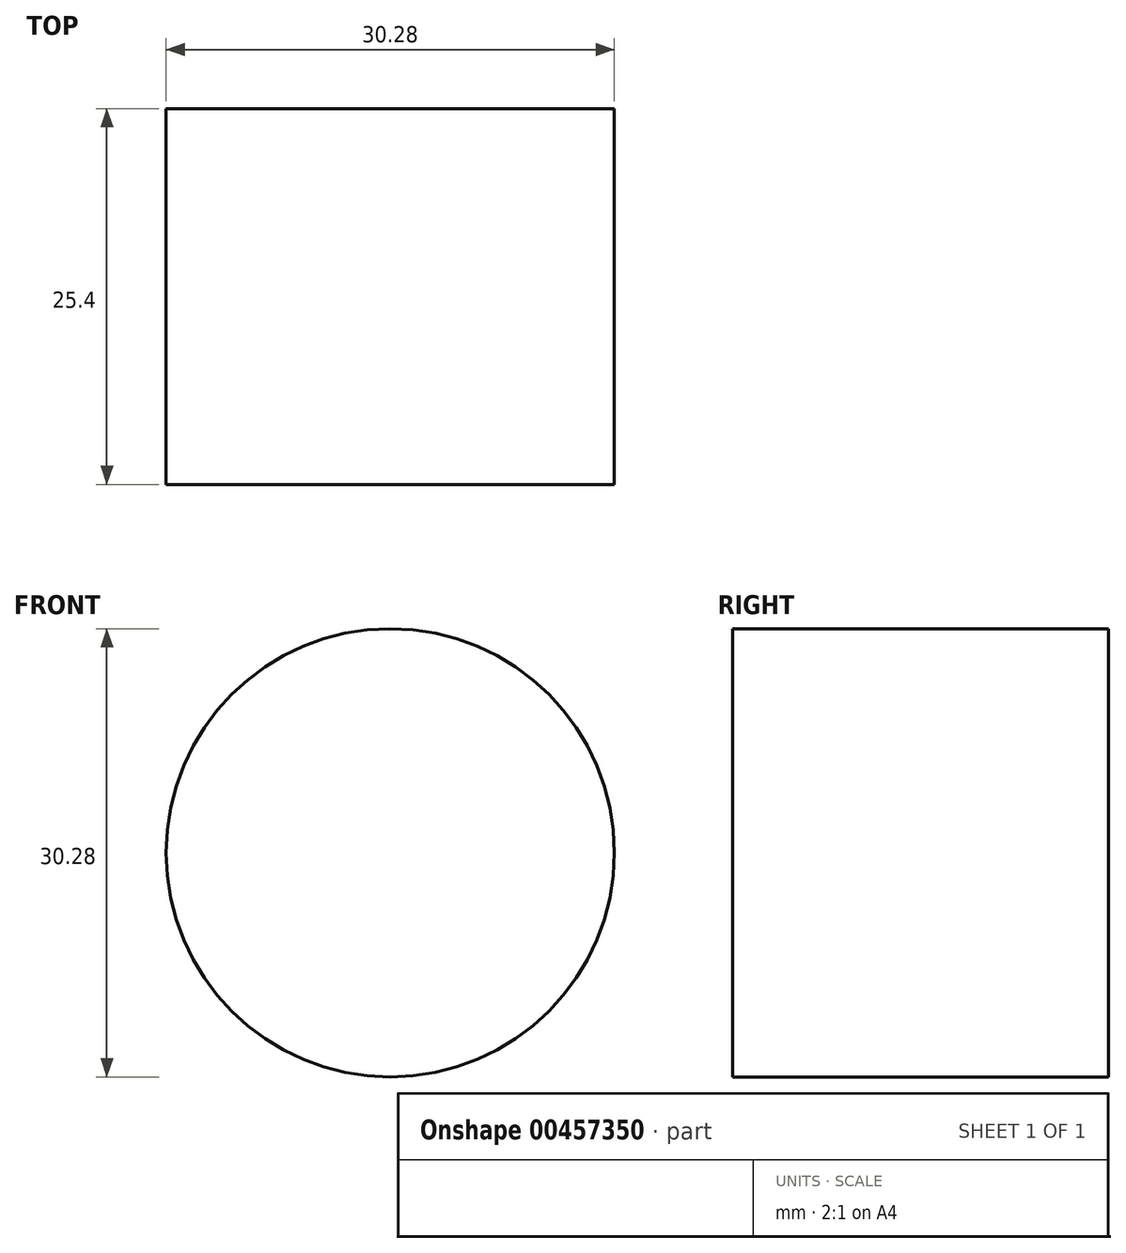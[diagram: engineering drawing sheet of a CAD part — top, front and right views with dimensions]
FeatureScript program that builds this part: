
annotation { "Feature Type Name" : "Feature", "Feature Type Description" : "" }
export const myFeature = defineFeature(function(context is Context, id is Id, definition is map)
    precondition{}
    {
        {
            var Q0;
            Q0=qCreatedBy(makeId("Front.planeOp"),FACE);
            var sketch = newSketch(context, id + "F0", { "sketchPlane" : qUnion([Q0])});
            skCircle(sketch, "E0", {"center": v(0, 0) * mm, "radius": 15.14 * mm});
            skSolve(sketch);
        }
        {
            var Q0;
            Q0=sQuery(id+"F0.wireOp",EDGE,"E0");
            extrude(context, id + "F1", {"bodyType" : ToolBodyType.SURFACE, "surfaceEntities" : qUnion([Q0]), "depth" : 25.4 * mm});
        }
    });
